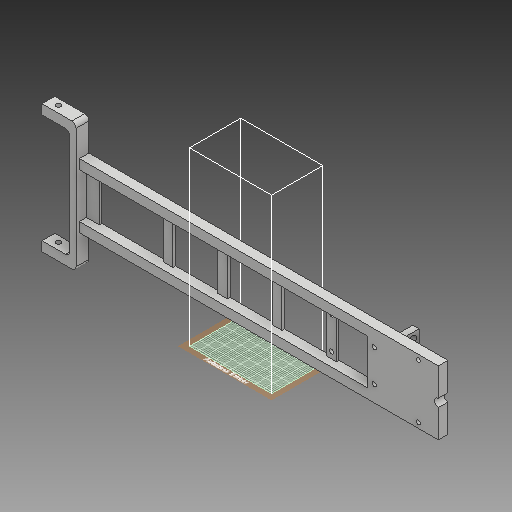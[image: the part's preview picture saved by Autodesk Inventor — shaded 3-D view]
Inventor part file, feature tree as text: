
AUTODESK INVENTOR PART (.ipt)
format: ipt  version: 2018 (Build 220112000, 112)  size: 904,704 bytes
history: native  units: mm
features: sketch x60, extrude x46, fillet x13, hole x6, plane x1
ambient origin geometry x8: Origin, YZ Plane, XZ Plane, XY Plane, X Axis, Y Axis, Z Axis, Center Point
bodies: Solid1 (feature_tree)
feature tree (126):
  extrude  "Extrusion1"  Depth=50.0mm
  hole  "Hole1"  [1 undecoded]
  hole  "Hole2"  [1 undecoded]
  extrude  "Extrusion2"  Depth=25.0mm
  extrude  "Extrusion3"  Depth=25.0mm
  extrude  "Extrusion4"  Depth=5.0mm
  sketch  "Sketch7"  dims[d25=10.0mm d26=5.0mm]
  extrude  "Extrusion5"  Depth=5.0mm
  extrude  "Extrusion6"  Depth=35.0mm
  extrude  "Extrusion7"  Depth=35.0mm
  extrude  "Extrusion8"  Depth=35.0mm
  extrude  "Extrusion9"  Depth=2.0mm TaperAngle=0.0deg
  extrude  "Extrusion10"  Depth=7.5mm TaperAngle=0.0deg
  extrude  "Extrusion11"  Depth=10.0mm
  extrude  "Extrusion12"  Depth=7.5mm
  fillet  "Fillet1"  Radius=7.5mm
  fillet  "Fillet2"  Radius=25.0mm
  fillet  "Fillet3"  Radius=3.0mm
  fillet  "Fillet4"  Radius=3.2mm
  fillet  "Fillet5"  Radius=2.1mm
  fillet  "Fillet6"  Radius=5.5mm
  extrude  "Extrusion13"  Depth=92.5mm TaperAngle=0.0deg
  sketch  "Sketch17"  dims[d58=4.25mm d59=241.0mm d60=0.0mm]
  hole  "Hole3"  [1 undecoded]
  hole  "Hole4"  [1 undecoded]
  extrude  "Extrusion14"  Depth=5.0mm
  extrude  "Extrusion15"  Depth=2.5mm TaperAngle=0.0deg
  extrude  "Extrusion16"  Depth=30.0mm
  extrude  "Extrusion17"  Depth=2.5mm
  extrude  "Extrusion18"  Depth=14.55mm TaperAngle=0.0deg
  extrude  "Extrusion19"  Depth=0.1mm
  extrude  "Extrusion20"  Depth=3.25mm
  extrude  "Extrusion21"  Depth=3.25mm
  hole  "Hole5"  [1 undecoded]
  extrude  "Extrusion22"  Depth=2.0mm
  extrude  "Extrusion23"  Depth=15.0mm
  extrude  "Extrusion24"  Depth=10.0mm TaperAngle=0.0deg
  hole  "Hole6"  [1 undecoded]
  extrude  "Extrusion25"  Depth=100.0mm TaperAngle=0.0deg
  extrude  "Extrusion26"  Depth=2.0mm TaperAngle=0.0deg
  sketch  "Sketch35"  dims[d116=3.3mm d117=3.3mm]
  plane  "Work Plane1"
  sketch  "Sketch36"  dims[d118=3.3mm d119=3.3mm d120=2.0mm d121=0.0mm]
  extrude  "Extrusion27"  Depth=3.3mm
  extrude  "Extrusion28"  Depth=2.0mm
  fillet  "Fillet7"  Radius=2.0mm
  extrude  "Extrusion29"  Depth=8.0mm
  extrude  "Extrusion30"  Depth=21.0mm
  extrude  "Extrusion31"  Depth=8.5mm
  extrude  "Extrusion32"  Depth=3.5mm
  sketch  "Sketch43"  dims[d142=10.0mm d143=0.0mm d144=7.5mm d145=0.0mm]
  fillet  "Fillet8"  Radius=3.3mm
  extrude  "Extrusion33"  Depth=3.3mm
  extrude  "Extrusion34"  Depth=7.5mm TaperAngle=0.0deg
  extrude  "Extrusion35"  Depth=15.0mm
  extrude  "Extrusion36"  Depth=100.0mm TaperAngle=0.0deg
  extrude  "Extrusion37"  Depth=5.0mm
  fillet  "Fillet9"  Radius=5.0mm
  fillet  "Fillet10"  Radius=37.5mm
  fillet  "Fillet11"  Radius=1.1mm
  fillet  "Fillet12"  Radius=37.5mm
  sketch  "Sketch49"  dims[d170=5.5mm d171=0.0mm d172=10.0mm d173=0.0mm]
  extrude  "Extrusion38"  Depth=3.0mm
  extrude  "Extrusion39"  Depth=10.0mm TaperAngle=0.0deg
  extrude  "Extrusion40"  Depth=74.724mm
  fillet  "Fillet13"  Radius=85.515mm
  extrude  "Extrusion41"  Depth=5.0mm
  extrude  "Extrusion42"  Depth=5.0mm
  sketch  "Sketch55"  dims[d186=10.0mm d187=2.0mm d188=0.0mm]
  extrude  "Extrusion43"  Depth=5.0mm
  extrude  "Extrusion44"  Depth=2.0mm TaperAngle=0.0deg
  sketch  "Sketch58"  dims[d194=10.0mm]
  extrude  "Extrusion45"  Depth=2.0mm TaperAngle=0.0deg
  extrude  "Extrusion46"  Depth=1.0mm TaperAngle=0.0deg
  sketch  "Sketch1"  dims[d0=50.0mm d1=50.0mm]
  sketch  "Sketch2"  dims[d2=240.0mm d3=7.5mm]
  sketch  "Sketch3"  dims[d4=7.5mm d5=7.5mm d6=0.0mm]
  sketch  "Sketch4"  dims[d7=6.35mm d8=6.0mm d9=4.0mm d10=2.0mm d11=90.0deg d12=8.0mm d13=20.594885mm d14=25.0mm]
  sketch  "Sketch5"  dims[d15=3.3mm d16=6.0mm d17=4.0mm d18=2.0mm d19=90.0deg d20=8.0mm d21=20.594885mm d22=25.0mm]
  sketch  "Sketch6"  dims[d23=180.0deg d24=5.0mm]
  sketch  "Sketch8"  dims[d27=17.5mm d28=0.0mm d30=35.0mm]
  sketch  "Sketch9"  dims[d31=35.0mm d32=35.0mm]
  sketch  "Sketch10"  dims[d33=35.0mm d34=35.0mm]
  sketch  "Sketch11"  dims[d35=35.0mm d36=2.0mm d37=0.0mm]
  sketch  "Sketch12"  dims[d38=10.0mm d39=7.5mm d40=0.0mm]
  sketch  "Sketch13"  dims[d41=100.0mm d42=10.0mm]
  sketch  "Sketch14"  dims[d43=7.5mm d44=0.0mm d45=7.5mm d46=7.5mm d47=25.0mm d48=0.0mm d49=3.0mm d50=3.2mm d51=2.1mm d52=5.5mm]
  sketch  "Sketch15"  dims[d53=3.3mm d54=92.5mm d55=0.0mm]
  sketch  "Sketch16"  dims[d56=5.5mm d57=3.3mm]
  sketch  "Sketch18"  dims[d61=4.44mm d62=5.0mm]
  sketch  "Sketch19"  dims[d63=2.5mm d64=91.25mm d65=0.0mm]
  sketch  "Sketch20"  dims[d66=30.0mm d67=6.35mm]
  sketch  "Sketch21"  dims[d68=3.8mm d69=0.0mm d70=2.5mm]
  sketch  "Sketch22"  dims[d71=14.55mm d72=0.0mm d73=14.55mm d74=0.0mm]
  sketch  "Sketch23"  dims[d75=0.1mm d76=0.1mm]
  sketch  "Sketch24"  dims[d77=3.25mm d78=3.25mm]
  sketch  "Sketch25"  dims[d79=3.25mm d80=3.25mm]
  sketch  "Sketch26"  dims[d81=35.0mm d82=10.0mm]
  sketch  "Sketch27"  dims[d83=2.0mm d84=0.0mm d85=3.6mm]
  sketch  "Sketch28"  dims[d86=3.6mm]
  sketch  "Sketch29"  dims[d87=3.3mm d88=6.0mm d89=4.0mm d90=2.0mm d91=90.0deg d92=15.0mm d93=20.594885mm]
  sketch  "Sketch30"  dims[d94=3.3mm d95=6.0mm d96=4.0mm d97=2.0mm d98=90.0deg d99=15.0mm d100=20.594885mm d101=6.0mm]
  sketch  "Sketch31"  dims[d102=20.0mm d103=0.0mm d104=10.0mm d105=0.0mm]
  sketch  "Sketch32"  dims[d106=2.0mm d107=0.0mm d108=4.0mm]
  sketch  "Sketch33"  dims[d109=100.0mm d110=0.0mm d111=100.0mm d112=0.0mm]
  sketch  "Sketch34"  dims[d113=5.0mm d114=2.0mm d115=0.0mm]
  sketch  "Sketch37"  dims[d122=5.5mm d123=0.0mm]
  sketch  "Sketch38"  dims[d124=3.3mm d125=6.0mm d126=4.0mm d127=2.0mm d128=90.0deg d129=8.0mm d130=20.594885mm d131=42.0mm]
  sketch  "Sketch39"  dims[d132=17.0mm d133=21.0mm]
  sketch  "Sketch40"  dims[d135=8.5mm d136=15.825mm]
  sketch  "Sketch41"  dims[d137=3.5mm d138=21.0mm d139=3.3mm]
  sketch  "Sketch42"  dims[d140=3.3mm d141=3.3mm]
  sketch  "Sketch44"  dims[d146=100.0mm d147=0.0mm]
  sketch  "Sketch45"  dims[d148=5.0mm d149=6.0mm d150=4.0mm d151=2.0mm d152=90.0deg d153=15.0mm d154=0.0mm d155=3.75mm]
  sketch  "Sketch46"  dims[d156=100.0mm d157=0.0mm d158=100.0mm d159=0.0mm]
  sketch  "Sketch47"  dims[d160=-0.698132mm d161=5.0mm d162=5.0mm d163=37.5mm d164=0.0mm d165=1.1mm d166=37.5mm d167=0.0mm]
  sketch  "Sketch48"  dims[d168=0.2mm d169=3.0mm]
  sketch  "Sketch50"  dims[d174=74.724mm d175=74.724mm d176=85.515mm]
  sketch  "Sketch51"  dims[d177=5.0mm d178=85.515mm]
  sketch  "Sketch52"  dims[d179=5.0mm d180=85.515mm]
  sketch  "Sketch53"  dims[d181=5.0mm d182=85.515mm]
  sketch  "Sketch54"  dims[d183=5.0mm d184=2.0mm d185=0.0mm]
  sketch  "Sketch56"  dims[d189=2.0mm d190=1.0mm d191=0.0mm]
  sketch  "Sketch57"  dims[d192=2.0mm d193=0.0mm]
  sketch  "Sketch59"  dims[d195=1.0mm d196=0.0mm]
  sketch  "Sketch60"  dims[d197=20.0mm d198=1.0mm d199=0.0mm d200=7.5mm d201=5.0mm d202=2.5mm d203=0.0mm d204=3.25mm d205=3.25mm d206=3.25mm d207=3.25mm d208=6.25mm d209=9.58mm d210=250.0mm d211=0.0mm d212=5.25mm d213=4.3mm d214=0.0mm d215=4.3mm d216=0.0mm d217=0.25mm d218=9.7mm d219=100.0mm d220=0.0mm d221=9.8mm d222=4.5mm d223=4.3mm d224=0.0mm d225=9.8mm d226=4.3mm d227=0.0mm d228=10.0mm d229=0.0mm d230=20.0mm d231=10.0mm d232=0.0mm d233=5.0mm d234=5.0mm d235=10.0mm d236=0.0mm]
note: 6 required parameter values undecoded (feature->parameter linkage not recoverable at this tier; creation-order binding heuristic only, values carry confidence <= 0.55)
